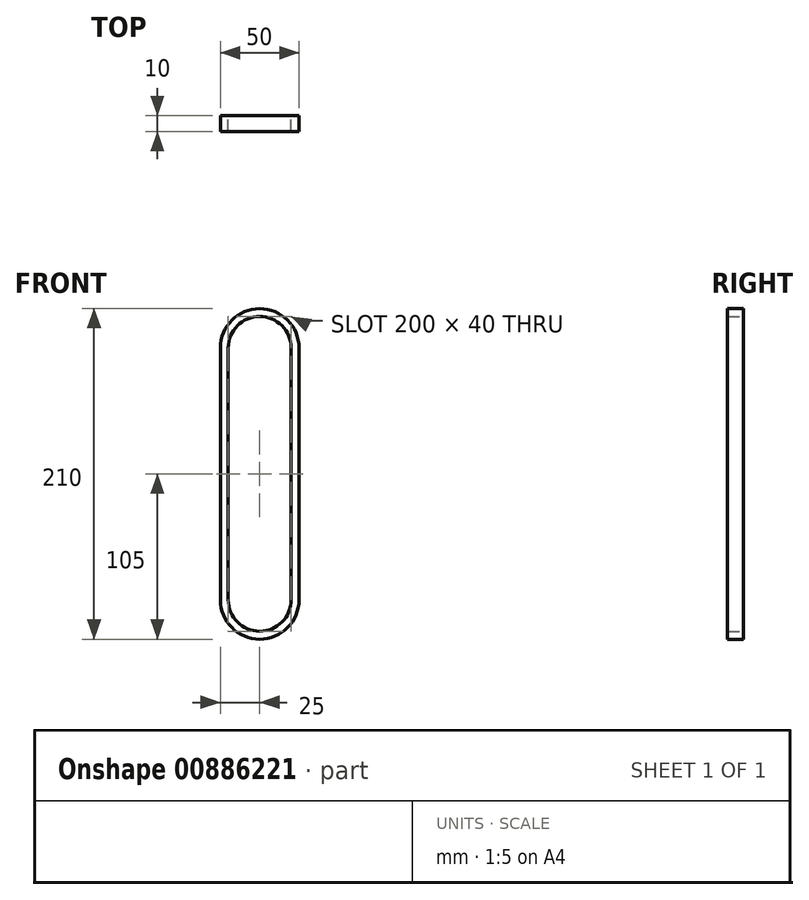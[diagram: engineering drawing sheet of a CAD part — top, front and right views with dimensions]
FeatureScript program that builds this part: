
annotation { "Feature Type Name" : "Feature", "Feature Type Description" : "" }
export const myFeature = defineFeature(function(context is Context, id is Id, definition is map)
    precondition{}
    {
        {
            var Q0;
            Q0=qCreatedBy(makeId("Front.planeOp"),FACE);
            var sketch = newSketch(context, id + "F0", { "sketchPlane" : qUnion([Q0])});
            skArc(sketch, "E0", {"start": v(20, 0) * mm, "mid": v(0, 20) * mm, "end": v(-20, 0) * mm});
            skLineSegment(sketch, "E1", {"start": v(0, 0) * mm, "end": v(0, -160) * mm});
            skArc(sketch, "E2", {"start": v(-25, -160) * mm, "mid": v(0, -185) * mm, "end": v(25, -160) * mm});
            skLineSegment(sketch, "E3", {"start": v(25, 0) * mm, "end": v(25, -160) * mm});
            skLineSegment(sketch, "E4", {"start": v(-25, 0) * mm, "end": v(-25, -160) * mm});
            skLineSegment(sketch, "E5", {"start": v(-20, 0) * mm, "end": v(-20, -160) * mm});
            skLineSegment(sketch, "E6", {"start": v(20, 0) * mm, "end": v(20, -160) * mm});
            skArc(sketch, "E7.trimOffspring", {"start": v(25, 0) * mm, "mid": v(0, 25) * mm, "end": v(-25, 0) * mm});
            skArc(sketch, "E8", {"start": v(-20, -160) * mm, "mid": v(0, -180) * mm, "end": v(20, -160) * mm});
            skSolve(sketch);
        }
        {
            var Q0;
            Q0 = qSketchRegion(id + "F0", true);
            extrude(context, id + "F1", {"entities" : qUnion([Q0]), "depth" : 10 * mm, "offsetDistance" : 25 * mm});
        }
    });
